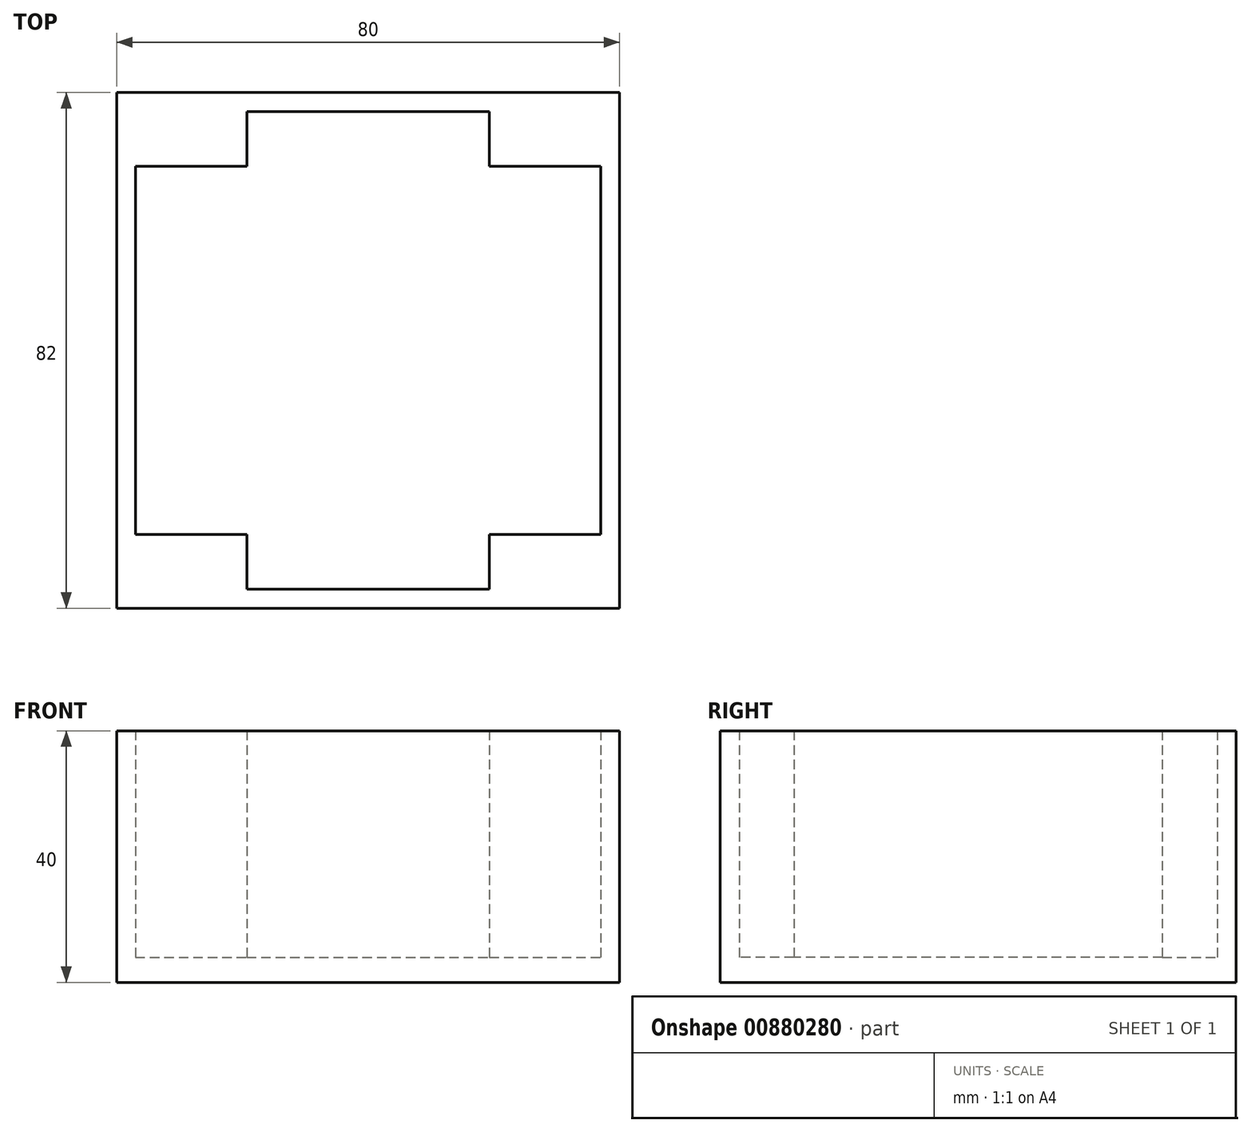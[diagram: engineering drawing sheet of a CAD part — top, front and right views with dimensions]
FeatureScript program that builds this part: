
annotation { "Feature Type Name" : "Feature", "Feature Type Description" : "" }
export const myFeature = defineFeature(function(context is Context, id is Id, definition is map)
    precondition{}
    {
        {
            var Q0;
            Q0=qCreatedBy(makeId("Top.planeOp"),FACE);
            var sketch = newSketch(context, id + "F0", { "sketchPlane" : qUnion([Q0])});
            skLineSegment(sketch, "E0.bottom", {"start": v(-40, 41) * mm, "end": v(40, 41) * mm});
            skLineSegment(sketch, "E0.top", {"start": v(-40, -41) * mm, "end": v(40, -41) * mm});
            skLineSegment(sketch, "E0.left", {"start": v(-40, 41) * mm, "end": v(-40, -41) * mm});
            skLineSegment(sketch, "E0.right", {"start": v(40, 41) * mm, "end": v(40, -41) * mm});
            skSolve(sketch);
        }
        {
            var Q0;
            Q0=makeQuery(id+"F0.imprint","IMPRINT",FACE,{"disambiguationData":[TD([[makeQuery(id+"F0.imprint","IMPRINT",EDGE,{"derivedFrom":sQuery(id+"F0.wireOp",EDGE,"E0.bottom")}),-1.0]])]});
            extrude(context, id + "F1", {"entities" : qUnion([Q0]), "depth" : 4 * mm, "offsetDistance" : 25 * mm});
        }
        {
            var Q0;
            Q0=makeQuery(id+"F1.opExtrude","CAP_FACE",FACE,{"disambiguationData":[OSD([sQuery(id+"F0.wireOp",EDGE,"E0.bottom"),sQuery(id+"F0.wireOp",EDGE,"E0.top"),sQuery(id+"F0.wireOp",EDGE,"E0.left"),sQuery(id+"F0.wireOp",EDGE,"E0.right")])],"isStart":false});
            var sketch = newSketch(context, id + "F2", { "sketchPlane" : qUnion([Q0])});
            skLineSegment(sketch, "E1", {"start": v(-19.3, 29.3) * mm, "end": v(-19.3, 38) * mm});
            skLineSegment(sketch, "E2", {"start": v(-19.3, 38) * mm, "end": v(19.3, 38) * mm});
            skLineSegment(sketch, "E3", {"start": v(19.3, 38) * mm, "end": v(19.3, 29.3) * mm});
            skLineSegment(sketch, "E4", {"start": v(19.3, 29.3) * mm, "end": v(37, 29.3) * mm});
            skLineSegment(sketch, "E5", {"start": v(37, 29.3) * mm, "end": v(37, -29.3) * mm});
            skLineSegment(sketch, "E6", {"start": v(37, -29.3) * mm, "end": v(19.3, -29.3) * mm});
            skLineSegment(sketch, "E7", {"start": v(19.3, -29.3) * mm, "end": v(19.3, -38) * mm});
            skLineSegment(sketch, "E8", {"start": v(19.3, -38) * mm, "end": v(-19.3, -38) * mm});
            skLineSegment(sketch, "E9", {"start": v(-19.3, -38) * mm, "end": v(-19.3, -29.3) * mm});
            skLineSegment(sketch, "E10", {"start": v(-19.3, -29.3) * mm, "end": v(-37, -29.3) * mm});
            skLineSegment(sketch, "E11", {"start": v(-37, -29.3) * mm, "end": v(-37, 29.3) * mm});
            skLineSegment(sketch, "E12", {"start": v(-37, 29.3) * mm, "end": v(-19.3, 29.3) * mm});
            skLineSegment(sketch, "E13.bottom", {"start": v(-40, 41) * mm, "end": v(40, 41) * mm});
            skLineSegment(sketch, "E13.top", {"start": v(-40, -41) * mm, "end": v(40, -41) * mm});
            skLineSegment(sketch, "E13.left", {"start": v(-40, 41) * mm, "end": v(-40, -41) * mm});
            skLineSegment(sketch, "E13.right", {"start": v(40, 41) * mm, "end": v(40, -41) * mm});
            skSolve(sketch);
        }
        {
            var Q0;
            Q0=makeQuery(id+"F2.imprint","IMPRINT",FACE,{"disambiguationData":[TD([[makeQuery(id+"F2.imprint","IMPRINT",EDGE,{"derivedFrom":sQuery(id+"F2.wireOp",EDGE,"E1")}),1.0]])]});
            extrude(context, id + "F3", {"entities" : qUnion([Q0]), "operationType" : NewBodyOperationType.ADD, "depth" : 36 * mm, "offsetDistance" : 25 * mm});
        }
    });
